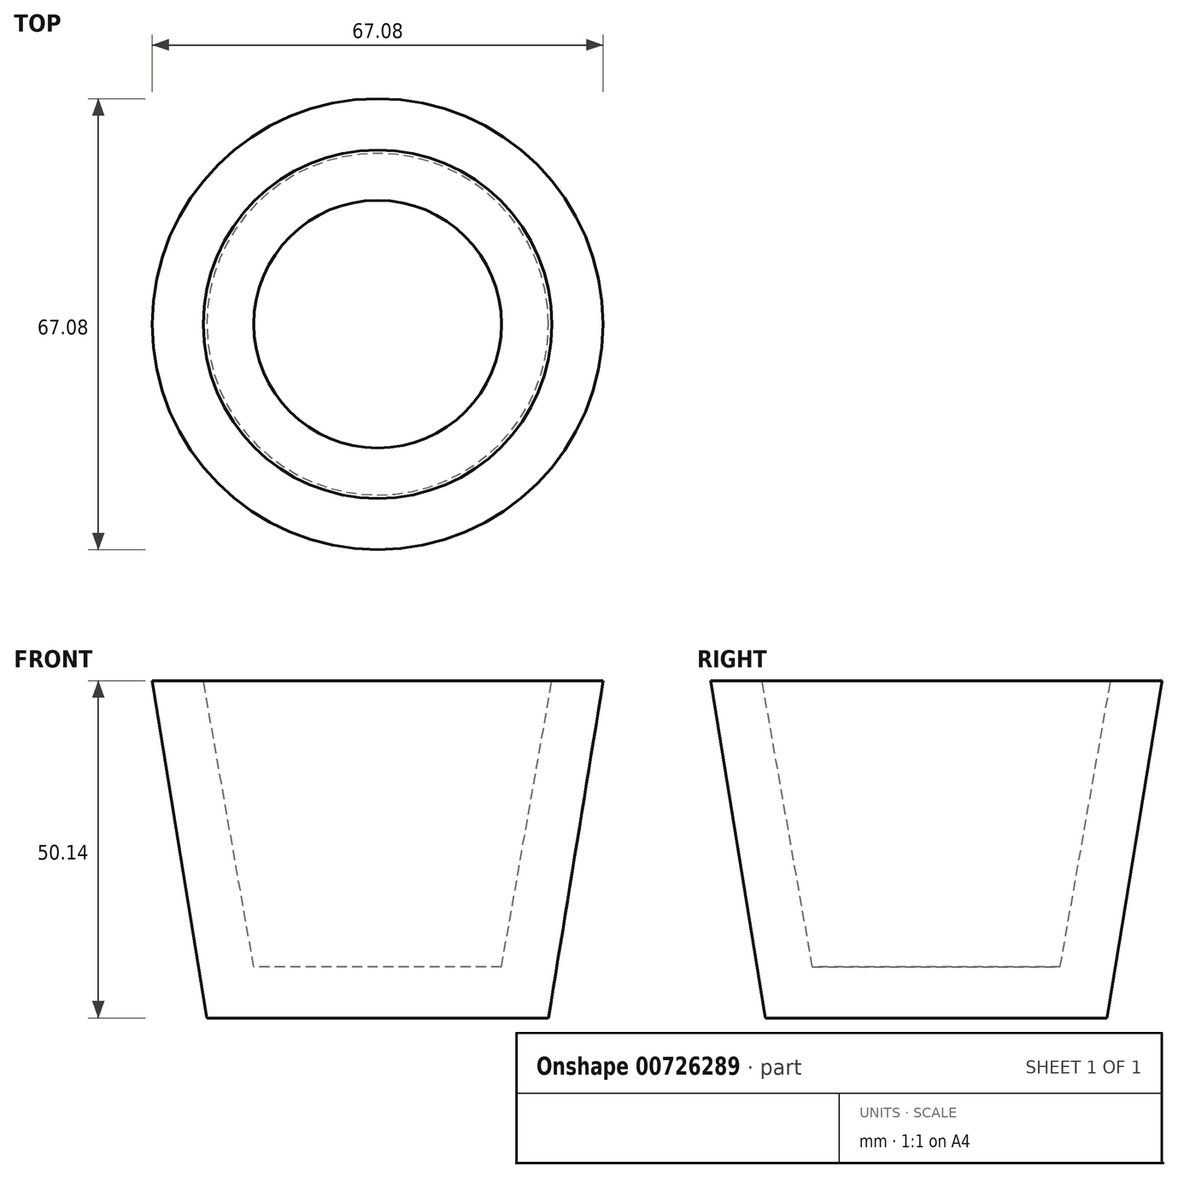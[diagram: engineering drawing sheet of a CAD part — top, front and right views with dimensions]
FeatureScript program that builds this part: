
annotation { "Feature Type Name" : "Feature", "Feature Type Description" : "" }
export const myFeature = defineFeature(function(context is Context, id is Id, definition is map)
    precondition{}
    {
        {
            var Q0;
            Q0=qCreatedBy(makeId("Right.planeOp"),FACE);
            var sketch = newSketch(context, id + "F0", { "sketchPlane" : qUnion([Q0])});
            skLineSegment(sketch, "E0", {"start": v(0, 0) * mm, "end": v(-25.4, 0) * mm});
            skLineSegment(sketch, "E1", {"start": v(-25.4, 0) * mm, "end": v(-33.54, 50.14) * mm});
            skLineSegment(sketch, "E2", {"start": v(-33.54, 50.14) * mm, "end": v(-25.92, 50.14) * mm});
            skLineSegment(sketch, "E3", {"start": v(-25.92, 50.14) * mm, "end": v(-18.42, 7.62) * mm});
            skLineSegment(sketch, "E4", {"start": v(-18.42, 7.62) * mm, "end": v(0, 7.62) * mm});
            skLineSegment(sketch, "E5", {"start": v(0, 7.62) * mm, "end": v(0, 0) * mm});
            skSolve(sketch);
        }
        {
            var Q0;
            Q0=makeQuery(id+"F0.imprint","IMPRINT",FACE,{"disambiguationData":[TD([[makeQuery(id+"F0.imprint","IMPRINT",EDGE,{"derivedFrom":sQuery(id+"F0.wireOp",EDGE,"E0")}),-1.0]])]});
            var Q1;
            Q1=sQuery(id+"F0.wireOp",EDGE,"E5");
            revolve(context, id + "F1", {"surfaceOperationType" : NewSurfaceOperationType.NEW, "entities" : qUnion([Q0]), "axis" : qUnion([Q1]), "revolveType" : RevolveType.FULL});
        }
    });
